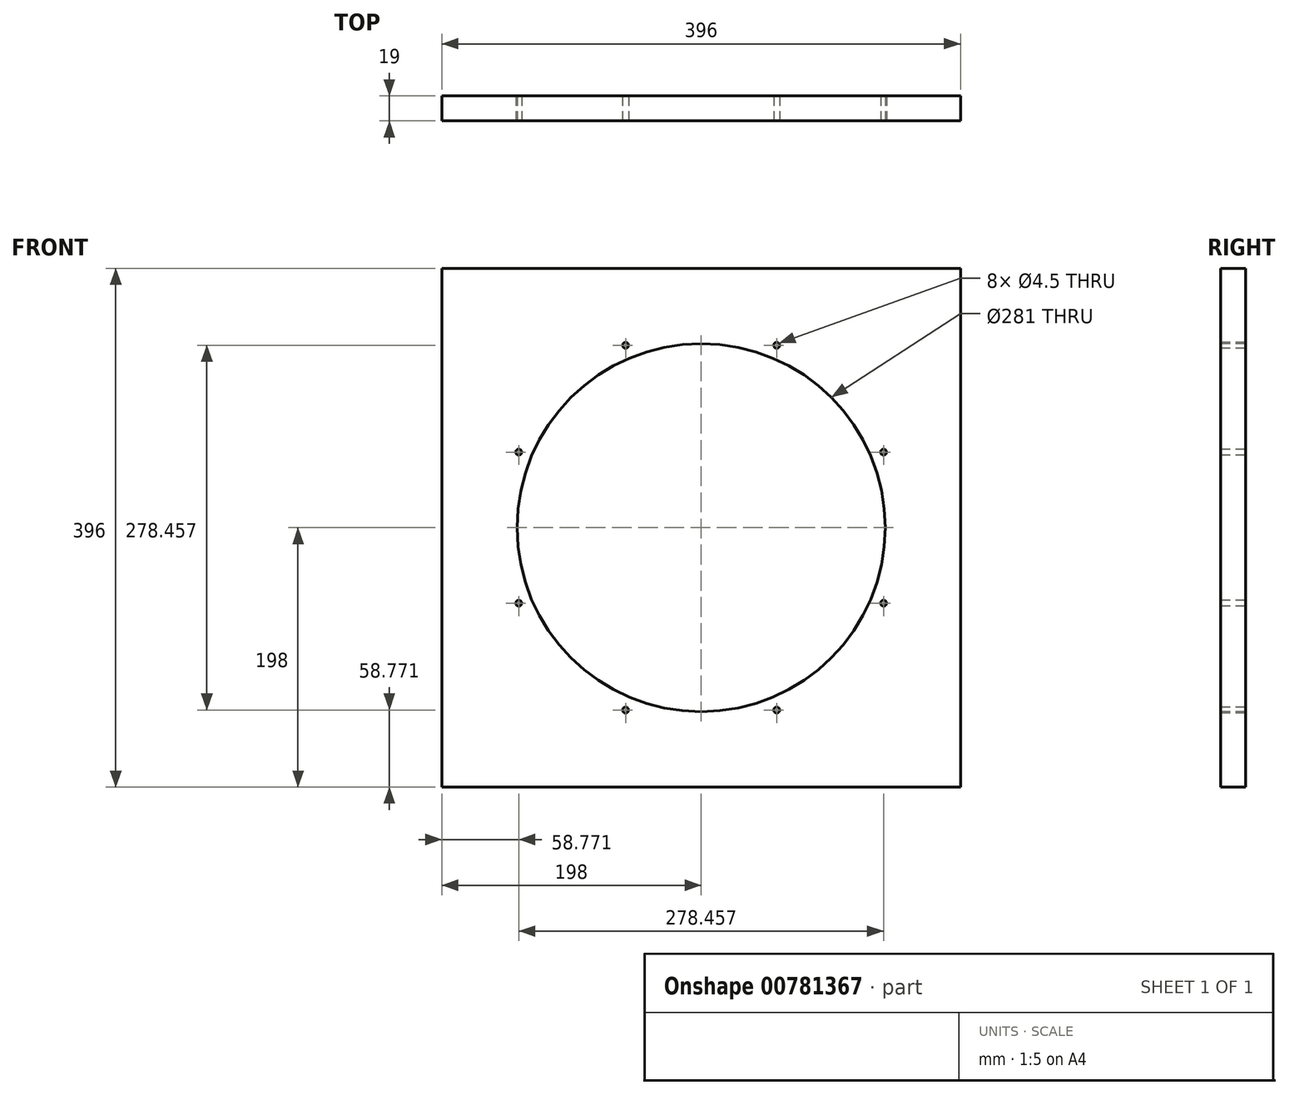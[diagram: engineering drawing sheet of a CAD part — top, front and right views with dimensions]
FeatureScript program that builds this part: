
annotation { "Feature Type Name" : "Feature", "Feature Type Description" : "" }
export const myFeature = defineFeature(function(context is Context, id is Id, definition is map)
    precondition{}
    {
        {
            var Q0;
            Q0=qCreatedBy(makeId("Front.planeOp"),FACE);
            var sketch = newSketch(context, id + "F0", { "sketchPlane" : qUnion([Q0])});
            skLineSegment(sketch, "E0.bottom", {"start": v(198, -198) * mm, "end": v(-198, -198) * mm});
            skLineSegment(sketch, "E0.top", {"start": v(198, 198) * mm, "end": v(-198, 198) * mm});
            skLineSegment(sketch, "E0.left", {"start": v(198, -198) * mm, "end": v(198, 198) * mm});
            skLineSegment(sketch, "E0.right", {"start": v(-198, -198) * mm, "end": v(-198, 198) * mm});
            skPoint(sketch, "E0.middle", {"position": v(0, 0) * mm});
            skSolve(sketch);
        }
        {
            var Q0;
            Q0=qSketchRegion(id+"F0",true);
            extrude(context, id + "F1", {"entities" : qUnion([Q0]), "depth" : 19 * mm, "offsetDistance" : 25.4 * mm});
        }
        {
            var Q0;
            Q0=makeQuery(id+"F1.opExtrude","CAP_FACE",FACE,{"disambiguationData":[OSD([sQuery(id+"F0.wireOp",EDGE,"E0.bottom"),sQuery(id+"F0.wireOp",EDGE,"E0.top"),sQuery(id+"F0.wireOp",EDGE,"E0.left"),sQuery(id+"F0.wireOp",EDGE,"E0.right")])],"isStart":false});
            var sketch = newSketch(context, id + "F2", { "sketchPlane" : qUnion([Q0])});
            skCircle(sketch, "E1", {"center": v(0, 0) * mm, "radius": 140.5 * mm});
            skSolve(sketch);
        }
        {
            var Q0;
            Q0=qSketchRegion(id+"F2",true);
            extrude(context, id + "F3", {"entities" : qUnion([Q0]), "operationType" : NewBodyOperationType.REMOVE, "oppositeDirection" : true, "depth" : 25.4 * mm, "offsetDistance" : 25.4 * mm});
        }
        {
            var Q0;
            Q0=makeQuery(id+"F1.opExtrude","CAP_FACE",FACE,{"disambiguationData":[OSD([sQuery(id+"F0.wireOp",EDGE,"E0.bottom"),sQuery(id+"F0.wireOp",EDGE,"E0.top"),sQuery(id+"F0.wireOp",EDGE,"E0.left"),sQuery(id+"F0.wireOp",EDGE,"E0.right")])],"isStart":false});
            var sketch = newSketch(context, id + "F4", { "sketchPlane" : qUnion([Q0])});
            skCircle(sketch, "E2", {"center": v(0, 0) * mm, "radius": 150.7 * mm, "construction": true});
            skLineSegment(sketch, "E3", {"start": v(0, 0) * mm, "end": v(0, 150.7) * mm, "construction": true});
            skLineSegment(sketch, "E4", {"start": v(0, 0) * mm, "end": v(57.67, 139.23) * mm, "construction": true});
            skLineSegment(sketch, "E5", {"start": v(0, 0) * mm, "end": v(139.23, 57.67) * mm, "construction": true});
            skLineSegment(sketch, "E6", {"start": v(0, 0) * mm, "end": v(139.23, -57.67) * mm, "construction": true});
            skLineSegment(sketch, "E7", {"start": v(0, 0) * mm, "end": v(57.67, -139.23) * mm, "construction": true});
            skLineSegment(sketch, "E8", {"start": v(0, 0) * mm, "end": v(-57.67, -139.23) * mm, "construction": true});
            skLineSegment(sketch, "E9", {"start": v(0, 0) * mm, "end": v(-139.23, -57.67) * mm, "construction": true});
            skLineSegment(sketch, "E10", {"start": v(0, 0) * mm, "end": v(-139.23, 57.67) * mm, "construction": true});
            skLineSegment(sketch, "E11", {"start": v(0, 0) * mm, "end": v(-57.67, 139.23) * mm, "construction": true});
            skCircle(sketch, "E12", {"center": v(57.67, 139.23) * mm, "radius": 2.25 * mm});
            skCircle(sketch, "E13", {"center": v(139.23, 57.67) * mm, "radius": 2.25 * mm});
            skCircle(sketch, "E14", {"center": v(139.23, -57.67) * mm, "radius": 2.25 * mm});
            skCircle(sketch, "E15", {"center": v(57.67, -139.23) * mm, "radius": 2.25 * mm});
            skCircle(sketch, "E16", {"center": v(-57.67, -139.23) * mm, "radius": 2.25 * mm});
            skCircle(sketch, "E17", {"center": v(-139.23, -57.67) * mm, "radius": 2.25 * mm});
            skCircle(sketch, "E18", {"center": v(-139.23, 57.67) * mm, "radius": 2.25 * mm});
            skCircle(sketch, "E19", {"center": v(-57.67, 139.23) * mm, "radius": 2.25 * mm});
            skSolve(sketch);
        }
        {
            var Q0;
            Q0=qSketchRegion(id+"F4",true);
            extrude(context, id + "F5", {"entities" : qUnion([Q0]), "operationType" : NewBodyOperationType.REMOVE, "oppositeDirection" : true, "depth" : 25.4 * mm, "offsetDistance" : 25.4 * mm});
        }
    });
